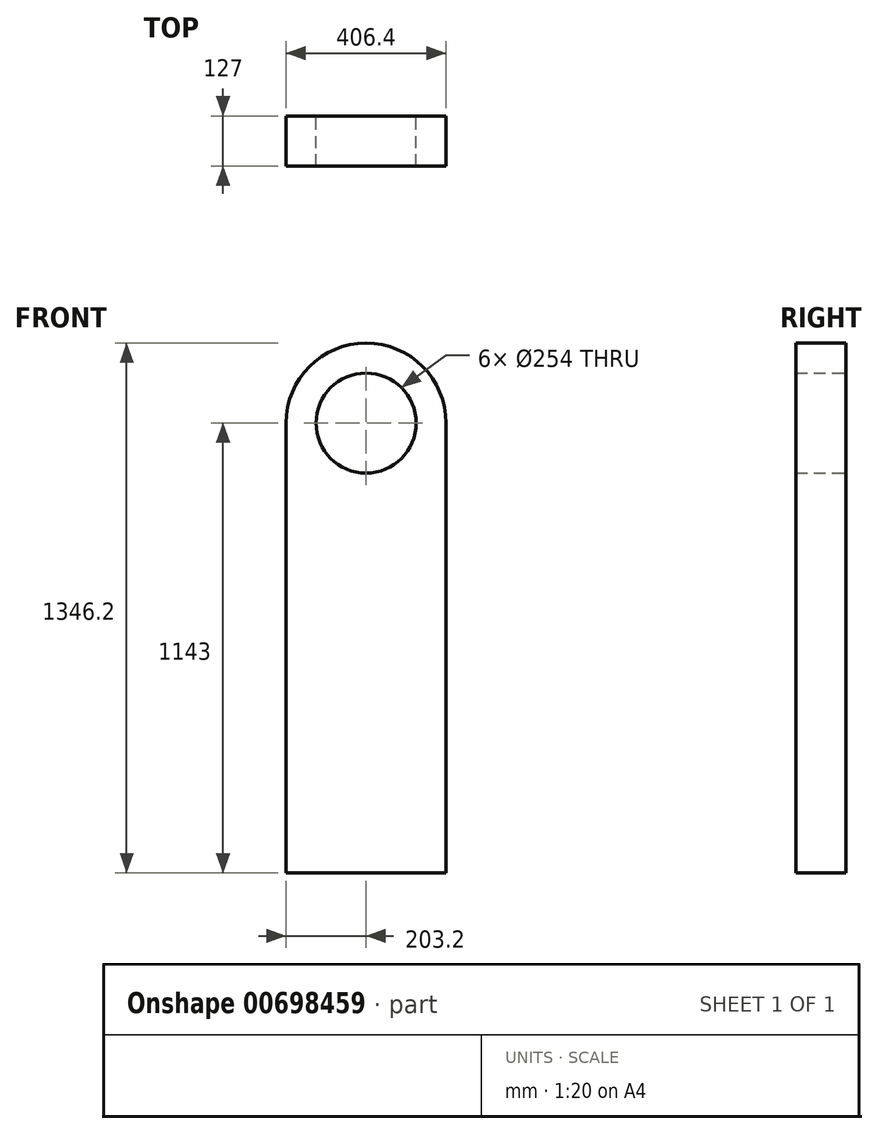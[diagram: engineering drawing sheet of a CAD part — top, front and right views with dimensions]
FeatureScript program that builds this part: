
annotation { "Feature Type Name" : "Feature", "Feature Type Description" : "" }
export const myFeature = defineFeature(function(context is Context, id is Id, definition is map)
    precondition{}
    {
        {
            var Q0;
            Q0=qCreatedBy(makeId("Front.planeOp"),FACE);
            var sketch = newSketch(context, id + "F0", { "sketchPlane" : qUnion([Q0])});
            skLineSegment(sketch, "E0.top", {"start": v(-203.2, -1143) * mm, "end": v(203.2, -1143) * mm});
            skLineSegment(sketch, "E0.left", {"start": v(-203.2, 0) * mm, "end": v(-203.2, -1143) * mm});
            skLineSegment(sketch, "E0.right", {"start": v(203.2, 0) * mm, "end": v(203.2, -1143) * mm});
            skArc(sketch, "E1", {"start": v(203.2, 0) * mm, "mid": v(0, 203.2) * mm, "end": v(-203.2, 0) * mm});
            skCircle(sketch, "E2", {"center": v(0, 0) * mm, "radius": 127 * mm});
            skSolve(sketch);
        }
        {
            var Q0;
            Q0=qSketchRegion(id+"F0",true);
            extrude(context, id + "F1", {"entities" : qUnion([Q0]), "endBound" : BoundingType.SYMMETRIC, "depth" : 127 * mm, "offsetDistance" : 25.4 * mm});
        }
    });
